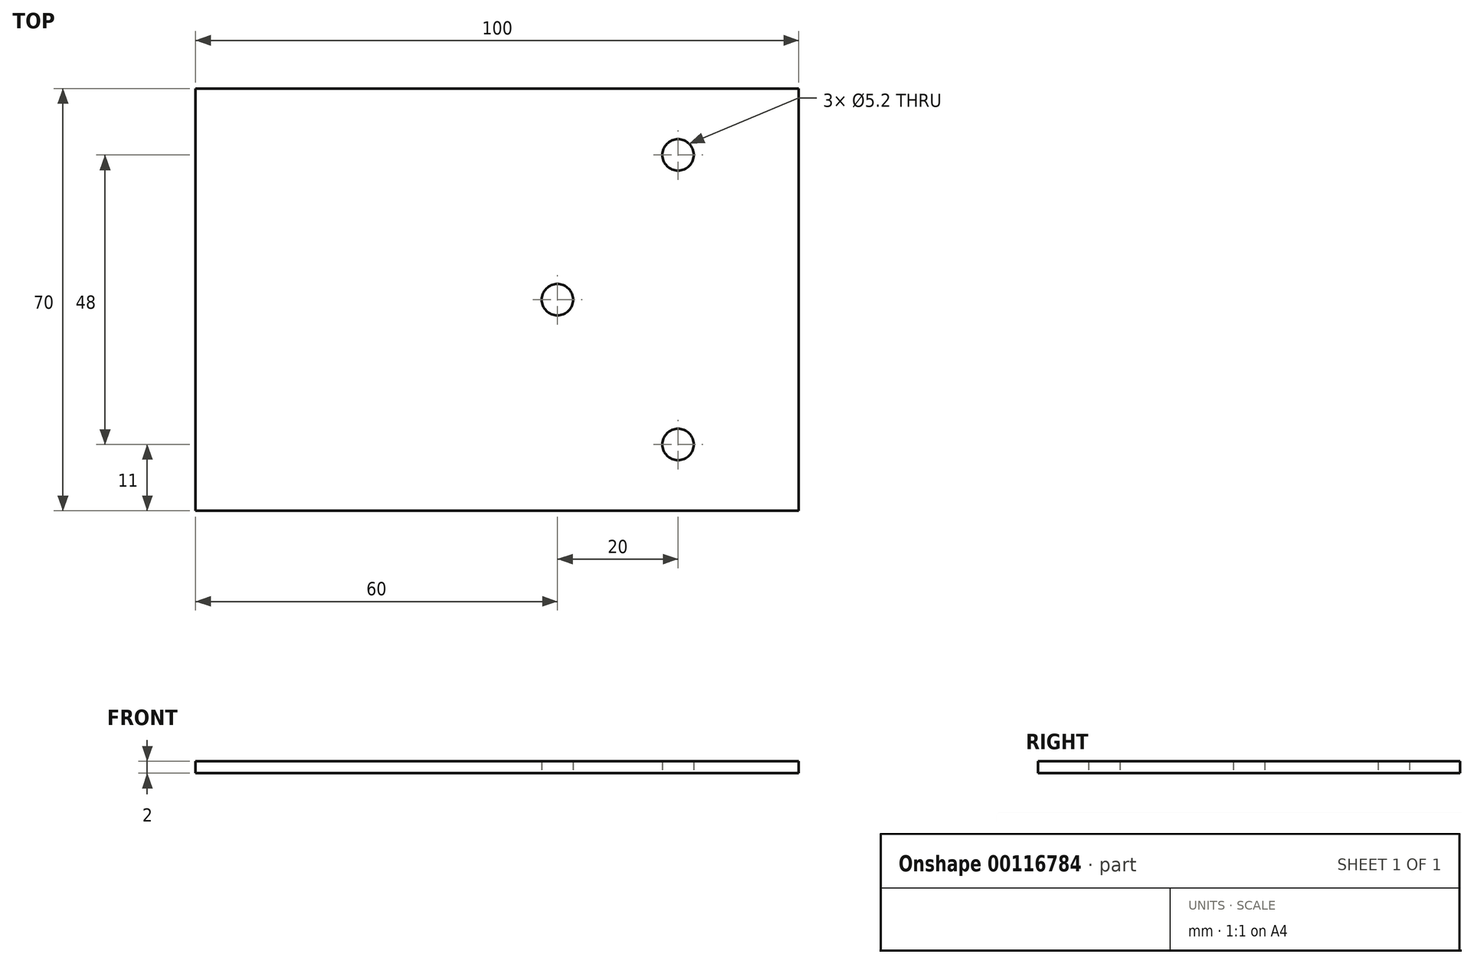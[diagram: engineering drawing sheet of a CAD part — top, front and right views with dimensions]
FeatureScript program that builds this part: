
annotation { "Feature Type Name" : "Feature", "Feature Type Description" : "" }
export const myFeature = defineFeature(function(context is Context, id is Id, definition is map)
    precondition{}
    {
        {
            var Q0;
            Q0=qCreatedBy(makeId("Top.planeOp"),FACE);
            var sketch = newSketch(context, id + "F0", { "sketchPlane" : qUnion([Q0])});
            skLineSegment(sketch, "E0.bottom", {"start": v(50, -35) * mm, "end": v(-50, -35) * mm});
            skLineSegment(sketch, "E0.top", {"start": v(50, 35) * mm, "end": v(-50, 35) * mm});
            skLineSegment(sketch, "E0.left", {"start": v(50, -35) * mm, "end": v(50, 35) * mm});
            skLineSegment(sketch, "E0.right", {"start": v(-50, -35) * mm, "end": v(-50, 35) * mm});
            skPoint(sketch, "E0.middle", {"position": v(0, 0) * mm});
            skCircle(sketch, "E1", {"center": v(30, 24) * mm, "radius": 2.6 * mm});
            skCircle(sketch, "E2", {"center": v(10, 0) * mm, "radius": 2.6 * mm});
            skCircle(sketch, "E3", {"center": v(30, -24) * mm, "radius": 2.6 * mm});
            skSolve(sketch);
        }
        {
            var Q0;
            Q0=makeQuery(id+"F0.imprint","IMPRINT",FACE,{"disambiguationData":[TD([[makeQuery(id+"F0.imprint","IMPRINT",EDGE,{"derivedFrom":sQuery(id+"F0.wireOp",EDGE,"E0.bottom")}),-1.0]])]});
            extrude(context, id + "F1", {"entities" : qUnion([Q0]), "depth" : 2 * mm});
        }
    });
